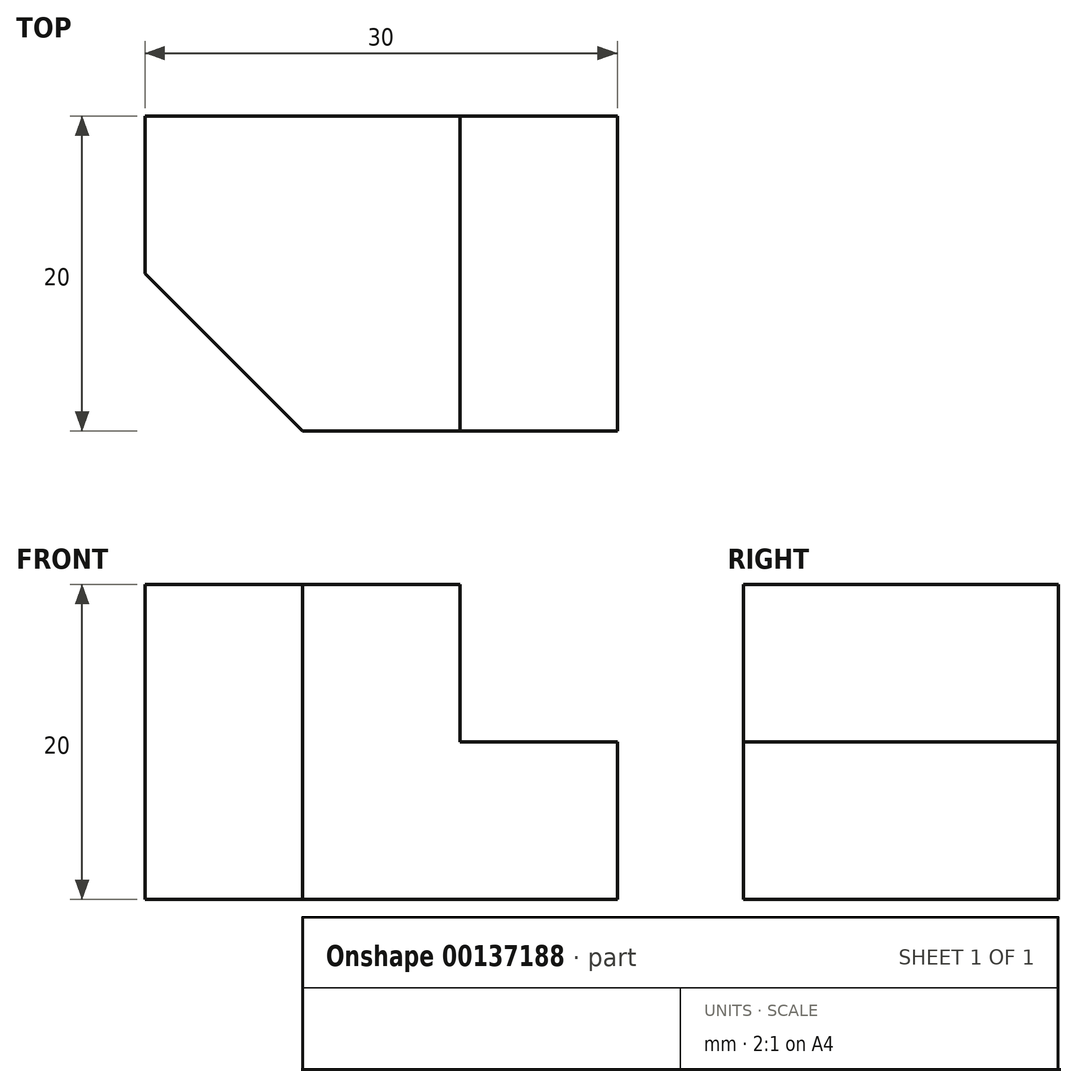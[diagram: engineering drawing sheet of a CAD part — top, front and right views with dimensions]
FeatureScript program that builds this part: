
annotation { "Feature Type Name" : "Feature", "Feature Type Description" : "" }
export const myFeature = defineFeature(function(context is Context, id is Id, definition is map)
    precondition{}
    {
        {
            var Q0;
            Q0=qCreatedBy(makeId("Front.planeOp"),FACE);
            var sketch = newSketch(context, id + "F0", { "sketchPlane" : qUnion([Q0])});
            skLineSegment(sketch, "E0", {"start": v(0, 0) * mm, "end": v(30, 0) * mm});
            skLineSegment(sketch, "E1", {"start": v(30, 0) * mm, "end": v(30, 10) * mm});
            skLineSegment(sketch, "E2", {"start": v(30, 10) * mm, "end": v(20, 10) * mm});
            skLineSegment(sketch, "E3", {"start": v(20, 10) * mm, "end": v(20, 20) * mm});
            skLineSegment(sketch, "E4", {"start": v(20, 20) * mm, "end": v(10, 20) * mm});
            skLineSegment(sketch, "E5", {"start": v(10, 20) * mm, "end": v(0, 20) * mm});
            skLineSegment(sketch, "E6", {"start": v(0, 20) * mm, "end": v(0, 0) * mm});
            skLineSegment(sketch, "E7", {"start": v(10, 20) * mm, "end": v(10, 0) * mm});
            skSolve(sketch);
        }
        {
            var Q0;
            Q0 = qSketchRegion(id + "F0", true);
            extrude(context, id + "F1", {"entities" : qUnion([Q0]), "endBound" : BoundingType.SYMMETRIC, "oppositeDirection" : true, "depth" : 20 * mm});
        }
        {
            var Q0;
            Q0=makeQuery(id+"F1.opExtrude","SWEPT_FACE",FACE,{"disambiguationData":[OSD([sQuery(id+"F0.wireOp",EDGE,"E4"),sQuery(id+"F0.wireOp",EDGE,"E5")])]});
            var sketch = newSketch(context, id + "F2", { "sketchPlane" : qUnion([Q0])});
            skLineSegment(sketch, "E8", {"start": v(10, -10) * mm, "end": v(0, 0) * mm});
            skSolve(sketch);
        }
        {
            var Q0;
            Q0 = qSketchRegion(id + "F2", true);
            var Q1;
            {var subQ0=sQuery(id+"F2.wireOp",EDGE,"E8");Q1=makeQuery(id+"F2.imprint","IMPRINT",FACE,{"disambiguationData":[TD([[makeQuery(id+"F2.imprint","IMPRINT",EDGE,{"derivedFrom":subQ0}),1.0]])]});}
            extrude(context, id + "F3", {"entities" : qUnion([Q0, Q1]), "operationType" : NewBodyOperationType.REMOVE, "endBound" : BoundingType.THROUGH_ALL, "oppositeDirection" : true, "depth" : 25 * mm});
        }
    });
